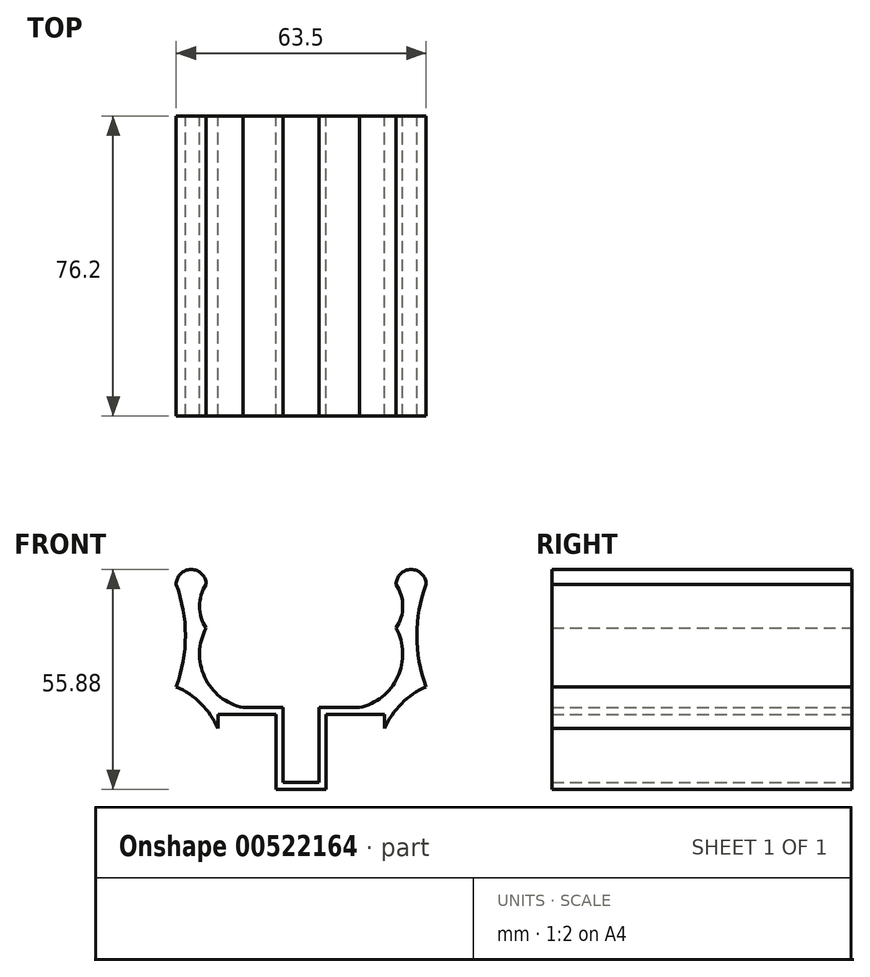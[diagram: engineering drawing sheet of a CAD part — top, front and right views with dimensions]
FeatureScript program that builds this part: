
annotation { "Feature Type Name" : "Feature", "Feature Type Description" : "" }
export const myFeature = defineFeature(function(context is Context, id is Id, definition is map)
    precondition{}
    {
        {
            var Q0;
            Q0=qCreatedBy(makeId("Front.planeOp"),FACE);
            var sketch = newSketch(context, id + "F0", { "sketchPlane" : qUnion([Q0])});
            skLineSegment(sketch, "E0", {"start": v(0, 0) * mm, "end": v(6.35, 0) * mm});
            skLineSegment(sketch, "E1", {"start": v(6.35, 0) * mm, "end": v(6.35, 19.05) * mm});
            skLineSegment(sketch, "E2", {"start": v(6.35, 19.05) * mm, "end": v(21.15, 19.05) * mm});
            skLineSegment(sketch, "E3", {"start": v(21.15, 19.05) * mm, "end": v(21.15, 15.5) * mm});
            skLineSegment(sketch, "E4", {"start": v(21.15, 15.5) * mm, "end": v(31.75, 26.1) * mm, "construction": true});
            skLineSegment(sketch, "E5", {"start": v(31.75, 26.1) * mm, "end": v(31.75, 55.88) * mm, "construction": true});
            skLineSegment(sketch, "E6", {"start": v(31.75, 55.88) * mm, "end": v(24.13, 55.88) * mm, "construction": true});
            skLineSegment(sketch, "E7", {"start": v(0, 1.78) * mm, "end": v(4.57, 1.78) * mm});
            skLineSegment(sketch, "E8", {"start": v(4.57, 1.78) * mm, "end": v(4.57, 20.83) * mm});
            skLineSegment(sketch, "E9", {"start": v(4.57, 20.83) * mm, "end": v(14.78, 20.83) * mm});
            skArc(sketch, "E10", {"start": v(31.75, 52.07) * mm, "mid": v(27.94, 55.88) * mm, "end": v(24.13, 52.07) * mm});
            skLineSegment(sketch, "E11", {"start": v(31.75, 40.99) * mm, "end": v(17.78, 40.99) * mm, "construction": true});
            skLineSegment(sketch, "E12", {"start": v(27.94, 52.07) * mm, "end": v(6.9, 52.07) * mm, "construction": true});
            skLineSegment(sketch, "E13", {"start": v(24.13, 54.92) * mm, "end": v(24.13, 9.9) * mm, "construction": true});
            skArc(sketch, "E14", {"start": v(14.78, 20.83) * mm, "mid": v(24.52, 28.56) * mm, "end": v(24.13, 40.99) * mm});
            skArc(sketch, "E15", {"start": v(24.13, 40.99) * mm, "mid": v(25.8, 46.53) * mm, "end": v(24.13, 52.07) * mm});
            skLineSegment(sketch, "E16", {"start": v(25.8, 57.18) * mm, "end": v(25.8, 23.48) * mm, "construction": true});
            skLineSegment(sketch, "E17", {"start": v(27.94, 52.07) * mm, "end": v(38.88, 52.07) * mm, "construction": true});
            skArc(sketch, "E18", {"start": v(31.75, 52.07) * mm, "mid": v(29.4, 39.08) * mm, "end": v(31.75, 26.1) * mm});
            skArc(sketch, "E19", {"start": v(31.75, 26.1) * mm, "mid": v(25.46, 21.78) * mm, "end": v(21.15, 15.5) * mm});
            skArc(sketch, "E20.MirrorCS", {"start": v(-31.75, 52.07) * mm, "mid": v(-29.4, 39.08) * mm, "end": v(-31.75, 26.1) * mm});
            skLineSegment(sketch, "E21.MirrorCS", {"start": v(-25.8, 57.18) * mm, "end": v(-25.8, 23.48) * mm, "construction": true});
            skLineSegment(sketch, "E22.MirrorCS", {"start": v(0, 0) * mm, "end": v(-6.35, 0) * mm});
            skLineSegment(sketch, "E23.MirrorCS", {"start": v(-6.35, 0) * mm, "end": v(-6.35, 19.05) * mm});
            skLineSegment(sketch, "E24.MirrorCS", {"start": v(-21.15, 19.05) * mm, "end": v(-21.15, 15.5) * mm});
            skArc(sketch, "E25.MirrorCS", {"start": v(-24.13, 40.99) * mm, "mid": v(-25.8, 46.53) * mm, "end": v(-24.13, 52.07) * mm});
            skLineSegment(sketch, "E26.MirrorCS", {"start": v(-31.75, 26.1) * mm, "end": v(-31.75, 55.88) * mm, "construction": true});
            skLineSegment(sketch, "E27.MirrorCS", {"start": v(-31.75, 55.88) * mm, "end": v(-24.13, 55.88) * mm, "construction": true});
            skLineSegment(sketch, "E28.MirrorCS", {"start": v(-21.15, 15.5) * mm, "end": v(-31.75, 26.1) * mm, "construction": true});
            skLineSegment(sketch, "E29.MirrorCS", {"start": v(-6.35, 19.05) * mm, "end": v(-21.15, 19.05) * mm});
            skArc(sketch, "E30.MirrorCS", {"start": v(-31.75, 26.1) * mm, "mid": v(-25.46, 21.78) * mm, "end": v(-21.15, 15.5) * mm});
            skLineSegment(sketch, "E31.MirrorCS", {"start": v(-24.13, 54.92) * mm, "end": v(-24.13, 9.9) * mm, "construction": true});
            skArc(sketch, "E32.MirrorCS", {"start": v(-31.75, 52.07) * mm, "mid": v(-27.94, 55.88) * mm, "end": v(-24.13, 52.07) * mm});
            skLineSegment(sketch, "E33.MirrorCS", {"start": v(-27.94, 52.07) * mm, "end": v(-6.9, 52.07) * mm, "construction": true});
            skLineSegment(sketch, "E34.MirrorCS", {"start": v(-31.75, 40.99) * mm, "end": v(-17.78, 40.99) * mm, "construction": true});
            skLineSegment(sketch, "E35.MirrorCS", {"start": v(-4.57, 20.83) * mm, "end": v(-14.78, 20.83) * mm});
            skLineSegment(sketch, "E36.MirrorCS", {"start": v(-4.57, 1.78) * mm, "end": v(-4.57, 20.83) * mm});
            skLineSegment(sketch, "E37.MirrorCS", {"start": v(0, 1.78) * mm, "end": v(-4.57, 1.78) * mm});
            skArc(sketch, "E38.MirrorCS", {"start": v(-14.78, 20.83) * mm, "mid": v(-24.52, 28.56) * mm, "end": v(-24.13, 40.99) * mm});
            skSolve(sketch);
        }
        {
            var Q0;
            Q0 = qSketchRegion(id + "F0", true);
            extrude(context, id + "F1", {"entities" : qUnion([Q0]), "depth" : 76.2 * mm, "offsetDistance" : 25.4 * mm});
        }
    });
